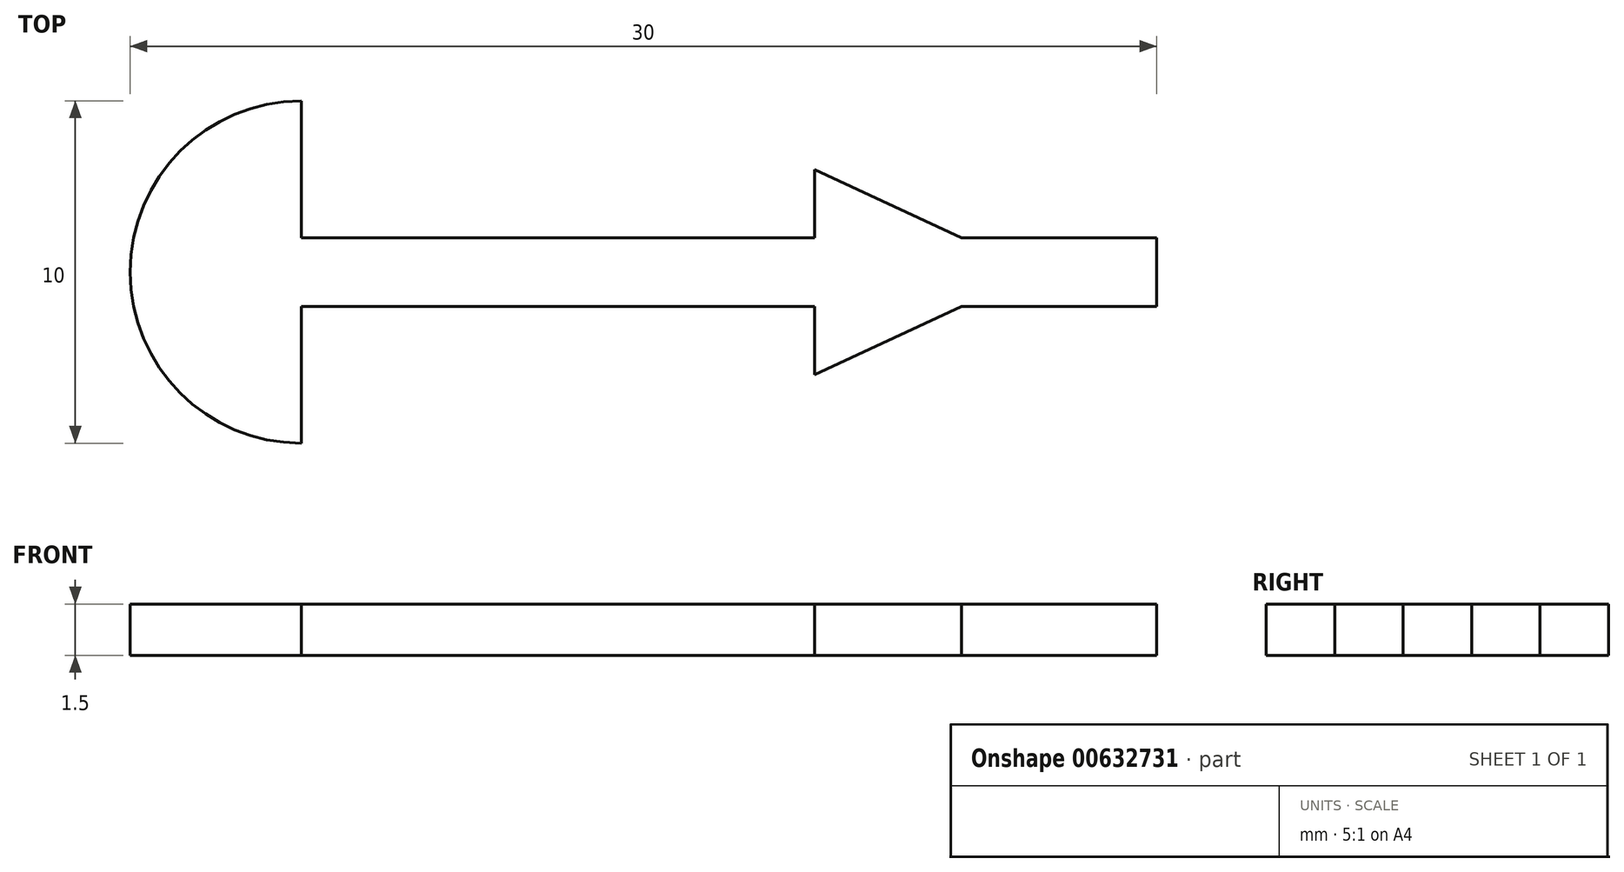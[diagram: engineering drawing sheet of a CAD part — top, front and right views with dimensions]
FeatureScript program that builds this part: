
annotation { "Feature Type Name" : "Feature", "Feature Type Description" : "" }
export const myFeature = defineFeature(function(context is Context, id is Id, definition is map)
    precondition{}
    {
        {
            var Q0;
            Q0=qCreatedBy(makeId("Top.planeOp"),FACE);
            var sketch = newSketch(context, id + "F0", { "sketchPlane" : qUnion([Q0])});
            skLineSegment(sketch, "E0.bottom", {"start": v(0, 1) * mm, "end": v(25, 1) * mm});
            skLineSegment(sketch, "E0.top", {"start": v(0, -1) * mm, "end": v(25, -1) * mm});
            skLineSegment(sketch, "E0.left", {"start": v(0, 1) * mm, "end": v(0, -1) * mm});
            skLineSegment(sketch, "E0.right", {"start": v(25, 1) * mm, "end": v(25, -1) * mm});
            skLineSegment(sketch, "E1", {"start": v(0, 5) * mm, "end": v(0, -5) * mm});
            skLineSegment(sketch, "E2", {"start": v(0, 0) * mm, "end": v(25, 0) * mm, "construction": true});
            skArc(sketch, "E3", {"start": v(0, 5) * mm, "mid": v(-5, 0) * mm, "end": v(0, -5) * mm});
            skLineSegment(sketch, "E4", {"start": v(15, -1) * mm, "end": v(15, -3) * mm});
            skLineSegment(sketch, "E5", {"start": v(15, -3) * mm, "end": v(19.29, -1) * mm});
            skLineSegment(sketch, "E6.MirrorCS", {"start": v(15, 1) * mm, "end": v(15, 3) * mm});
            skLineSegment(sketch, "E7.MirrorCS", {"start": v(15, 3) * mm, "end": v(19.29, 1) * mm});
            skSolve(sketch);
        }
        {
            var Q0;
            Q0=qSketchRegion(id+"F0",true);
            extrude(context, id + "F1", {"entities" : qUnion([Q0]), "depth" : 1.5 * mm});
        }
    });
